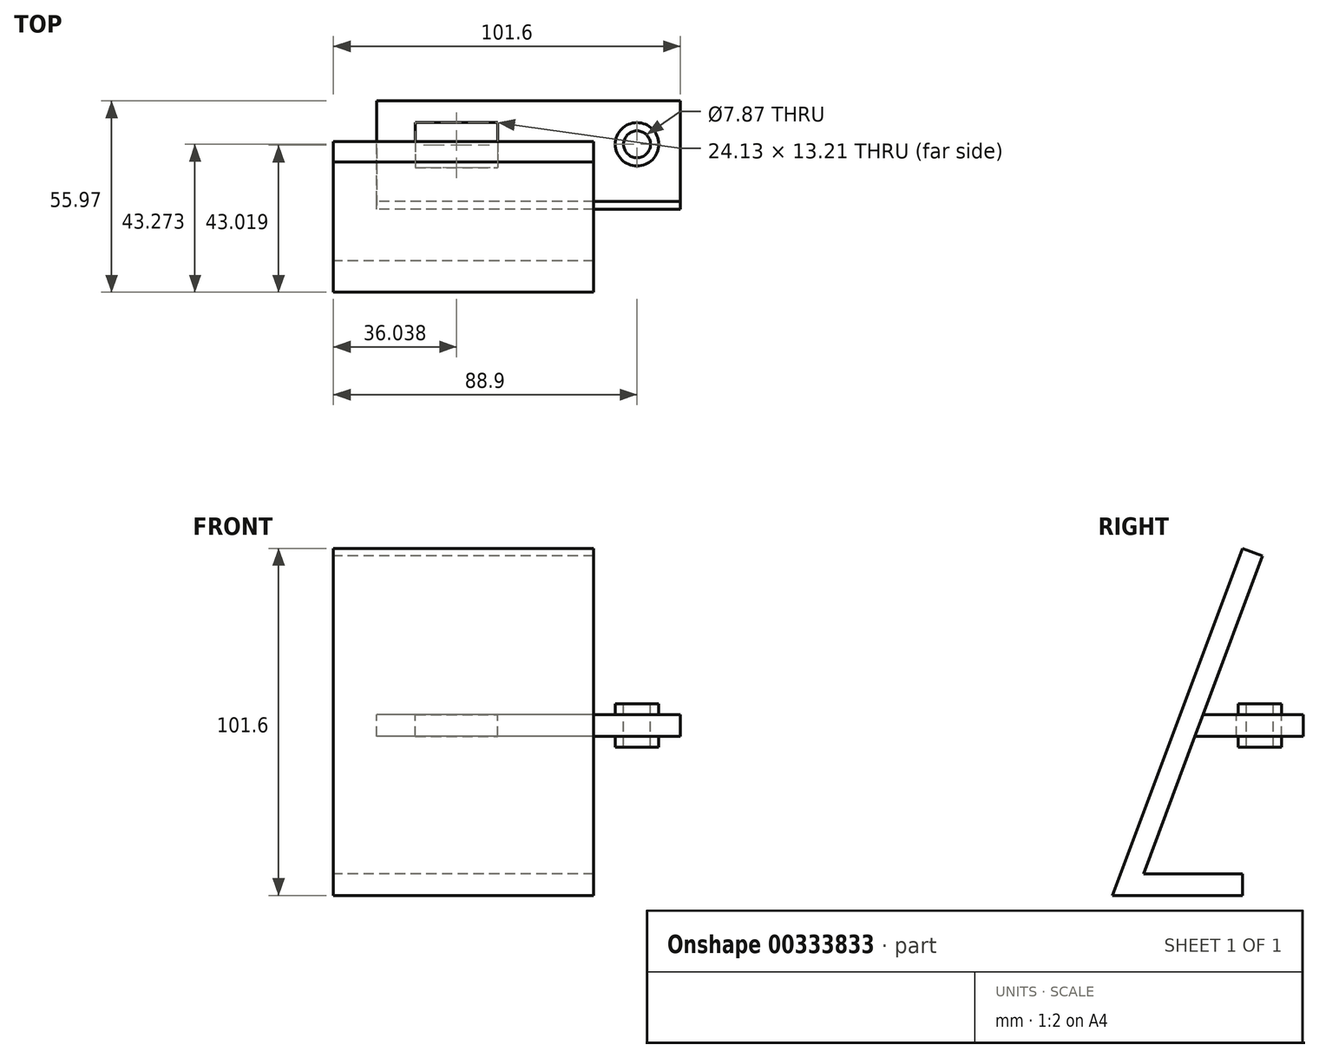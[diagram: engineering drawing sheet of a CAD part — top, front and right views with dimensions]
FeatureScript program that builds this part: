
annotation { "Feature Type Name" : "Feature", "Feature Type Description" : "" }
export const myFeature = defineFeature(function(context is Context, id is Id, definition is map)
    precondition{}
    {
        {
            var Q0;
            Q0=qCreatedBy(makeId("Right.planeOp"),FACE);
            var sketch = newSketch(context, id + "F0", { "sketchPlane" : qUnion([Q0])});
            skLineSegment(sketch, "E0", {"start": v(0, 0) * mm, "end": v(-38.1, 0) * mm});
            skLineSegment(sketch, "E1", {"start": v(-38.1, 0) * mm, "end": v(0, 101.6) * mm});
            skLineSegment(sketch, "E2.0", {"start": v(-28.94, 6.35) * mm, "end": v(5.95, 99.37) * mm});
            skLineSegment(sketch, "E2.1", {"start": v(0, 6.35) * mm, "end": v(-28.94, 6.35) * mm});
            skLineSegment(sketch, "E3", {"start": v(0, 101.6) * mm, "end": v(5.95, 99.37) * mm});
            skLineSegment(sketch, "E4", {"start": v(0, 6.35) * mm, "end": v(0, 0) * mm});
            skLineSegment(sketch, "E5", {"start": v(-11.5, 52.86) * mm, "end": v(17.87, 52.86) * mm});
            skLineSegment(sketch, "E6", {"start": v(17.87, 52.86) * mm, "end": v(17.87, 46.51) * mm});
            skLineSegment(sketch, "E7", {"start": v(17.87, 46.51) * mm, "end": v(-13.88, 46.51) * mm});
            skSolve(sketch);
        }
        {
            var Q0;
            Q0=makeQuery(id+"F0.imprint","IMPRINT",FACE,{"disambiguationData":[TD([[makeQuery(id+"F0.imprint","IMPRINT",EDGE,{"derivedFrom":sQuery(id+"F0.wireOp",EDGE,"E0")}),-1.0]])]});
            extrude(context, id + "F1", {"entities" : qUnion([Q0]), "endBound" : BoundingType.SYMMETRIC, "depth" : 76.2 * mm});
        }
        {
            var Q0;
            {var subQ0=sQuery(id+"F0.wireOp",EDGE,"E5");Q0=makeQuery(id+"F0.imprint","IMPRINT",FACE,{"disambiguationData":[TD([[makeQuery(id+"F0.imprint","IMPRINT",EDGE,{"derivedFrom":subQ0}),-1.0]])]});}
            extrude(context, id + "F2", {"entities" : qUnion([Q0]), "operationType" : NewBodyOperationType.ADD, "endBound" : BoundingType.SYMMETRIC, "depth" : 50.8 * mm});
        }
        {
            var Q0;
            Q0=makeQuery(id+"F2.opExtrude","CAP_FACE",FACE,{"disambiguationData":[OSD([sQuery(id+"F0.wireOp",EDGE,"E2.0"),sQuery(id+"F0.wireOp",EDGE,"E5"),sQuery(id+"F0.wireOp",EDGE,"E6"),sQuery(id+"F0.wireOp",EDGE,"E7")])],"isStart":false});
            extrude(context, id + "F3", {"entities" : qUnion([Q0]), "operationType" : NewBodyOperationType.ADD, "depth" : 38.1 * mm});
        }
        {
            var Q0;
            {var subQ0=sQuery(id+"F0.wireOp",EDGE,"E5");Q0=makeQuery(id+"F3.boolean.opBoolean","MERGE",FACE,{"derivedFrom":[makeQuery(id+"F2.opExtrude","SWEPT_FACE",FACE,{"disambiguationData":[OSD([subQ0])]}),makeQuery(id+"F3.opExtrude","SWEPT_FACE",FACE,{"disambiguationData":[OSD([subQ0])]})]});}
            var sketch = newSketch(context, id + "F4", { "sketchPlane" : qUnion([Q0])});
            skCircle(sketch, "E8", {"center": v(50.8, 5.17) * mm, "radius": 3.94 * mm});
            skCircle(sketch, "E9", {"center": v(50.8, 5.17) * mm, "radius": 6.35 * mm});
            skSolve(sketch);
        }
        {
            var Q0;
            Q0=makeQuery(id+"F4.imprint","IMPRINT",FACE,{"disambiguationData":[TD([[makeQuery(id+"F4.imprint","IMPRINT",EDGE,{"derivedFrom":sQuery(id+"F4.wireOp",EDGE,"E8")}),1.0]])]});
            var Q1;
            {var subQ0=sQuery(id+"F0.wireOp",EDGE,"E7");Q1=makeQuery(id+"F3.boolean.opBoolean","MERGE",FACE,{"derivedFrom":[makeQuery(id+"F2.opExtrude","SWEPT_FACE",FACE,{"disambiguationData":[OSD([subQ0])]}),makeQuery(id+"F3.opExtrude","SWEPT_FACE",FACE,{"disambiguationData":[OSD([subQ0])]})]});}
            extrude(context, id + "F5", {"entities" : qUnion([Q0]), "operationType" : NewBodyOperationType.REMOVE, "endBound" : BoundingType.UP_TO_SURFACE, "oppositeDirection" : true, "endBoundEntityFace" : qUnion([Q1]), "depth" : 25.4 * mm});
        }
        {
            var Q0;
            Q0=makeQuery(id+"F4.imprint","IMPRINT",FACE,{"disambiguationData":[TD([[makeQuery(id+"F4.imprint","IMPRINT",EDGE,{"derivedFrom":sQuery(id+"F4.wireOp",EDGE,"E8")}),-1.0]])]});
            extrude(context, id + "F6", {"entities" : qUnion([Q0]), "operationType" : NewBodyOperationType.ADD, "depth" : 3.17 * mm});
        }
        {
            var Q0;
            Q0=makeQuery(id+"F6.opExtrude","CAP_FACE",FACE,{"disambiguationData":[OSD([sQuery(id+"F4.wireOp",EDGE,"E8"),sQuery(id+"F4.wireOp",EDGE,"E9")])],"isStart":false});
            extrude(context, id + "F7", {"entities" : qUnion([Q0]), "operationType" : NewBodyOperationType.ADD, "oppositeDirection" : true, "depth" : 12.7 * mm});
        }
        {
            var Q0;
            Q0=makeQuery(id+"F4.imprint","IMPRINT",FACE,{"disambiguationData":[TD([[makeQuery(id+"F4.imprint","IMPRINT",EDGE,{"derivedFrom":sQuery(id+"F4.wireOp",EDGE,"E9")}),-1.0]])]});
            var sketch = newSketch(context, id + "F8", { "sketchPlane" : qUnion([Q0])});
            skLineSegment(sketch, "E10.bottom", {"start": v(-14.13, 11.52) * mm, "end": v(10, 11.52) * mm});
            skLineSegment(sketch, "E10.top", {"start": v(-14.13, -1.68) * mm, "end": v(10, -1.68) * mm});
            skLineSegment(sketch, "E10.left", {"start": v(-14.13, 11.52) * mm, "end": v(-14.13, -1.68) * mm});
            skLineSegment(sketch, "E10.right", {"start": v(10, 11.52) * mm, "end": v(10, -1.68) * mm});
            skSolve(sketch);
        }
        {
            var Q0;
            Q0=makeQuery(id+"F8.imprint","IMPRINT",FACE,{"disambiguationData":[TD([[makeQuery(id+"F8.imprint","IMPRINT",EDGE,{"derivedFrom":sQuery(id+"F8.wireOp",EDGE,"E10.bottom")}),-1.0]])]});
            var Q1;
            {var subQ0=sQuery(id+"F0.wireOp",EDGE,"E7");Q1=makeQuery(id+"F3.boolean.opBoolean","MERGE",FACE,{"derivedFrom":[makeQuery(id+"F2.opExtrude","SWEPT_FACE",FACE,{"disambiguationData":[OSD([subQ0])]}),makeQuery(id+"F3.opExtrude","SWEPT_FACE",FACE,{"disambiguationData":[OSD([subQ0])]})]});}
            extrude(context, id + "F9", {"entities" : qUnion([Q0]), "operationType" : NewBodyOperationType.REMOVE, "endBound" : BoundingType.UP_TO_SURFACE, "oppositeDirection" : true, "endBoundEntityFace" : qUnion([Q1]), "depth" : 25.4 * mm});
        }
    });
